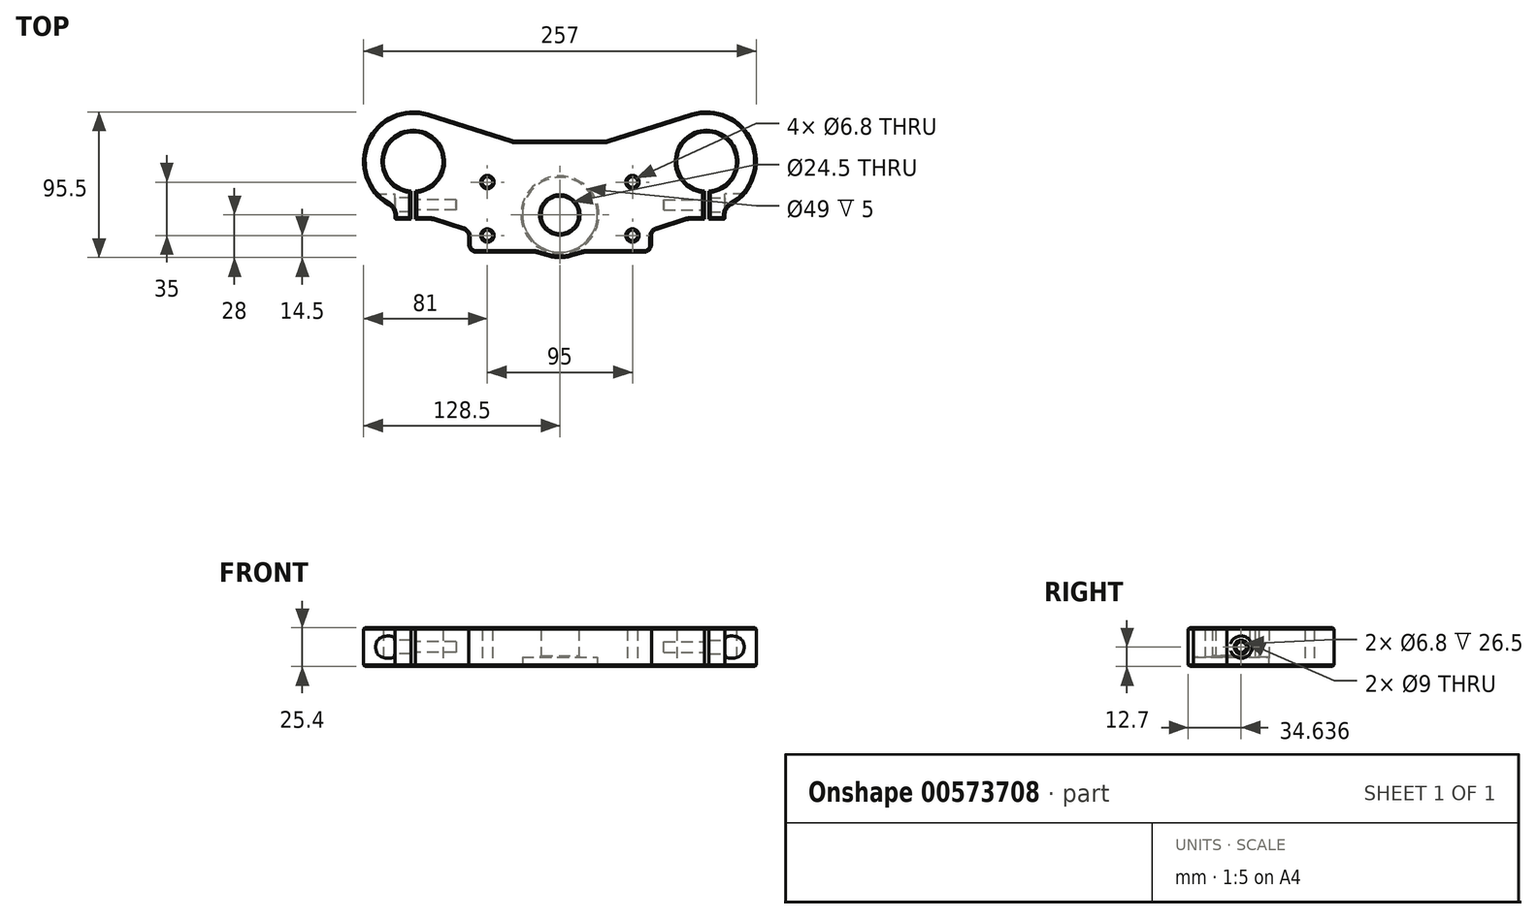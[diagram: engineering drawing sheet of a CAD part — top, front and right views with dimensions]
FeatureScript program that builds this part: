
annotation { "Feature Type Name" : "Feature", "Feature Type Description" : "" }
export const myFeature = defineFeature(function(context is Context, id is Id, definition is map)
    precondition{}
    {
        {
            var Q0;
            Q0=qCreatedBy(makeId("Top.planeOp"),FACE);
            var sketch = newSketch(context, id + "F0", { "sketchPlane" : qUnion([Q0])});
            skArc(sketch, "E0", {"start": v(-115.44, 16) * mm, "mid": v(-109.79, 3.71) * mm, "end": v(-97.5, -1.94) * mm});
            skArc(sketch, "E1", {"start": v(115.44, 19) * mm, "mid": v(82.21, 31.29) * mm, "end": v(94.5, -1.94) * mm});
            skCircle(sketch, "E2", {"center": v(0, -17.5) * mm, "radius": 12.25 * mm});
            skArc(sketch, "E3", {"start": v(108, -12.7) * mm, "mid": v(118.98, -5.48) * mm, "end": v(126.2, 5.5) * mm});
            skArc(sketch, "E4", {"start": v(-8.42, -44.2) * mm, "mid": v(0, -45.5) * mm, "end": v(8.42, -44.2) * mm});
            skLineSegment(sketch, "E5", {"start": v(-84, -20.36) * mm, "end": v(-59.7, -28.03) * mm});
            skLineSegment(sketch, "E6", {"start": v(84, -20.36) * mm, "end": v(59.9, -27.96) * mm});
            skLineSegment(sketch, "E7", {"start": v(-96, 17.5) * mm, "end": v(-150.04, 17.5) * mm, "construction": true});
            skLineSegment(sketch, "E8", {"start": v(-86.22, 48.5) * mm, "end": v(-29.97, 30.75) * mm});
            skLineSegment(sketch, "E9", {"start": v(86.22, 48.5) * mm, "end": v(29.97, 30.75) * mm});
            skLineSegment(sketch, "E10", {"start": v(-29.97, 30.75) * mm, "end": v(29.97, 30.75) * mm});
            skCircle(sketch, "E11", {"center": v(-47.5, 4) * mm, "radius": 3.4 * mm});
            skCircle(sketch, "E12", {"center": v(47.5, 4) * mm, "radius": 3.4 * mm});
            skCircle(sketch, "E13", {"center": v(-47.5, -31) * mm, "radius": 3.4 * mm});
            skCircle(sketch, "E14", {"center": v(47.5, -31) * mm, "radius": 3.4 * mm});
            skPoint(sketch, "E15.orphan", {"position": v(-108.6, 29.5) * mm});
            skPoint(sketch, "E16.orphan", {"position": v(-108.6, 5.5) * mm});
            skArc(sketch, "E17.trimOffspring", {"start": v(-86.22, 48.5) * mm, "mid": v(-109.95, 46.86) * mm, "end": v(-126.2, 29.5) * mm});
            skPoint(sketch, "E18.orphan", {"position": v(-148.56, 0) * mm});
            skPoint(sketch, "E19.MirrorCS.end.orphan", {"position": v(108.6, 5.5) * mm});
            skPoint(sketch, "E19.MirrorCS.start.orphan", {"position": v(108.6, 29.5) * mm});
            skArc(sketch, "E20.trimOffspring", {"start": v(-126.2, 5.5) * mm, "mid": v(-118.98, -5.48) * mm, "end": v(-108, -12.7) * mm});
            skArc(sketch, "E21.trimOffspring", {"start": v(126.2, 29.5) * mm, "mid": v(109.95, 46.86) * mm, "end": v(86.22, 48.5) * mm});
            skLineSegment(sketch, "E22", {"start": v(-47.5, 4) * mm, "end": v(-47.5, -31.88) * mm, "construction": true});
            skLineSegment(sketch, "E23", {"start": v(-47.5, -31.88) * mm, "end": v(95.24, -31.88) * mm, "construction": true});
            skLineSegment(sketch, "E24", {"start": v(-47.5, 4) * mm, "end": v(-47.5, 60.65) * mm, "construction": true});
            skLineSegment(sketch, "E25", {"start": v(47.5, -31) * mm, "end": v(47.5, 56.36) * mm, "construction": true});
            skLineSegment(sketch, "E26", {"start": v(-47.5, 36.28) * mm, "end": v(47.5, 36.28) * mm, "construction": true});
            skPoint(sketch, "E26.startSnap0", {"position": v(-47.5, 32.32) * mm});
            skLineSegment(sketch, "E27", {"start": v(-57.1, -42) * mm, "end": v(-15.4, -42) * mm});
            skLineSegment(sketch, "E28.trimOffspring", {"start": v(15.4, -42) * mm, "end": v(57.1, -42) * mm});
            skLineSegment(sketch, "E29.trimOffspring", {"start": v(-15.4, -42) * mm, "end": v(-8.42, -44.2) * mm});
            skLineSegment(sketch, "E30.trimOffspring", {"start": v(-47.5, -34.4) * mm, "end": v(-47.5, -34.52) * mm, "construction": true});
            skLineSegment(sketch, "E31.trimOffspring", {"start": v(15.4, -42) * mm, "end": v(8.42, -44.2) * mm});
            skArc(sketch, "E32", {"start": v(-126.2, 29.5) * mm, "mid": v(-128.5, 17.5) * mm, "end": v(-126.2, 5.5) * mm});
            skPoint(sketch, "E33.left.start.orphan", {"position": v(-134.5, 29.5) * mm});
            skPoint(sketch, "E33.top.start.orphan", {"position": v(-134.5, 5.5) * mm});
            skArc(sketch, "E34", {"start": v(-115.44, 19) * mm, "mid": v(-115.5, 17.5) * mm, "end": v(-115.44, 16) * mm});
            skArc(sketch, "E35", {"start": v(115.44, 19) * mm, "mid": v(115.49, 18.25) * mm, "end": v(115.5, 17.5) * mm});
            skArc(sketch, "E36", {"start": v(126.2, 29.5) * mm, "mid": v(128.5, 17.5) * mm, "end": v(126.2, 5.5) * mm});
            skArc(sketch, "E37", {"start": v(115.44, 16) * mm, "mid": v(115.49, 16.75) * mm, "end": v(115.5, 17.5) * mm});
            skLineSegment(sketch, "E38", {"start": v(-96, 17.5) * mm, "end": v(-96, -58.97) * mm, "construction": true});
            skLineSegment(sketch, "E39.top", {"start": v(-108, -20.36) * mm, "end": v(-97.5, -20.36) * mm});
            skLineSegment(sketch, "E39.left", {"start": v(-108, -12.7) * mm, "end": v(-108, -20.36) * mm});
            skLineSegment(sketch, "E40.MirrorCS", {"start": v(108, -20.36) * mm, "end": v(97.5, -20.36) * mm});
            skLineSegment(sketch, "E41.MirrorCS", {"start": v(108, -12.7) * mm, "end": v(108, -20.36) * mm});
            skPoint(sketch, "E42.orphan", {"position": v(105.78, -13.5) * mm});
            skLineSegment(sketch, "E43.left", {"start": v(-97.5, -1.94) * mm, "end": v(-97.5, -20.36) * mm});
            skLineSegment(sketch, "E43.right", {"start": v(-94.5, -1.94) * mm, "end": v(-94.5, -20.36) * mm});
            skLineSegment(sketch, "E44.left", {"start": v(94.5, -1.94) * mm, "end": v(94.5, -20.36) * mm});
            skLineSegment(sketch, "E44.right", {"start": v(97.5, -1.94) * mm, "end": v(97.5, -20.36) * mm});
            skLineSegment(sketch, "E45", {"start": v(96, 17.5) * mm, "end": v(96, -38.63) * mm, "construction": true});
            skPoint(sketch, "E45.endSnap0", {"position": v(96, -20.36) * mm});
            skArc(sketch, "E46.trimOffspring", {"start": v(-94.5, -1.94) * mm, "mid": v(-82.21, 31.29) * mm, "end": v(-115.44, 19) * mm});
            skLineSegment(sketch, "E47.trimOffspring", {"start": v(-94.5, -20.36) * mm, "end": v(-84, -20.36) * mm});
            skLineSegment(sketch, "E48.trimOffspring", {"start": v(94.5, -20.36) * mm, "end": v(84, -20.36) * mm});
            skArc(sketch, "E49.trimOffspring", {"start": v(97.5, -1.94) * mm, "mid": v(109.79, 3.71) * mm, "end": v(115.44, 16) * mm});
            skLineSegment(sketch, "E50", {"start": v(-57.1, -42) * mm, "end": v(-59.7, -42) * mm});
            skLineSegment(sketch, "E51", {"start": v(-59.7, -42) * mm, "end": v(-59.7, -28.03) * mm});
            skLineSegment(sketch, "E52", {"start": v(57.1, -42) * mm, "end": v(59.9, -42) * mm});
            skLineSegment(sketch, "E53", {"start": v(59.9, -42) * mm, "end": v(59.9, -27.96) * mm});
            skPoint(sketch, "E54.orphan", {"position": v(57.1, -28.85) * mm});
            skSolve(sketch);
        }
        {
            var Q0;
            Q0 = qSketchRegion(id + "F0", true);
            extrude(context, id + "F1", {"entities" : qUnion([Q0]), "depth" : 25.4 * mm, "offsetDistance" : 25 * mm});
        }
        {
            var Q0;
            Q0=makeQuery(id+"F1.opExtrude","CAP_FACE",FACE,{"disambiguationData":[OSD([sQuery(id+"F0.wireOp",EDGE,"E0"),sQuery(id+"F0.wireOp",EDGE,"E1"),sQuery(id+"F0.wireOp",EDGE,"E2"),sQuery(id+"F0.wireOp",EDGE,"E3"),sQuery(id+"F0.wireOp",EDGE,"E4"),sQuery(id+"F0.wireOp",EDGE,"E5"),sQuery(id+"F0.wireOp",EDGE,"E6"),sQuery(id+"F0.wireOp",EDGE,"E33.bottom"),sQuery(id+"F0.wireOp",EDGE,"E33.top"),sQuery(id+"F0.wireOp",EDGE,"E33.left"),sQuery(id+"F0.wireOp",EDGE,"f1757bc2-bd20-4476-96d3-2265b81b4f2b0.MirrorCS"),sQuery(id+"F0.wireOp",EDGE,"775a69b1-2f4f-49db-8b7b-db785da90cee0.MirrorCS"),sQuery(id+"F0.wireOp",EDGE,"3ec31bf6-936d-4883-9dcf-82827e0fa2ad0.MirrorCS"),sQuery(id+"F0.wireOp",EDGE,"E8"),sQuery(id+"F0.wireOp",EDGE,"E9"),sQuery(id+"F0.wireOp",EDGE,"E10"),sQuery(id+"F0.wireOp",EDGE,"E11"),sQuery(id+"F0.wireOp",EDGE,"E12"),sQuery(id+"F0.wireOp",EDGE,"E13"),sQuery(id+"F0.wireOp",EDGE,"E14"),sQuery(id+"F0.wireOp",EDGE,"E17.trimOffspring"),sQuery(id+"F0.wireOp",EDGE,"dbH54HY8-ATN7-0WNP-fYwK-wR0IxBY40SBz.bottom"),sQuery(id+"F0.wireOp",EDGE,"dbH54HY8-ATN7-0WNP-fYwK-wR0IxBY40SBz.top"),sQuery(id+"F0.wireOp",EDGE,"3AyZsfYV-9XAQ-6Yzz-t8sR-OLsTKYj4z3ro.bottom"),sQuery(id+"F0.wireOp",EDGE,"3AyZsfYV-9XAQ-6Yzz-t8sR-OLsTKYj4z3ro.top"),sQuery(id+"F0.wireOp",EDGE,"b436fade-894c-4302-851f-ed3abdfff13f.trimOffspring"),sQuery(id+"F0.wireOp",EDGE,"E20.trimOffspring"),sQuery(id+"F0.wireOp",EDGE,"c79fd97f-b23e-4375-80a9-bfeef2d48203.trimOffspring"),sQuery(id+"F0.wireOp",EDGE,"E21.trimOffspring")])],"isStart":true});
            var sketch = newSketch(context, id + "F2", { "sketchPlane" : qUnion([Q0])});
            skCircle(sketch, "E55", {"center": v(0, 17.5) * mm, "radius": 24.5 * mm});
            skSolve(sketch);
        }
        {
            var Q0;
            Q0 = qSketchRegion(id + "F2", true);
            extrude(context, id + "F3", {"entities" : qUnion([Q0]), "operationType" : NewBodyOperationType.REMOVE, "oppositeDirection" : true, "depth" : 6 * mm, "offsetDistance" : 25 * mm});
        }
        {
            var Q0;
            Q0=makeQuery(id+"F1.opExtrude","SWEPT_FACE",FACE,{"disambiguationData":[OSD([sQuery(id+"F0.wireOp",EDGE,"E39.left")])]});
            var sketch = newSketch(context, id + "F4", { "sketchPlane" : qUnion([Q0])});
            skCircle(sketch, "E56", {"center": v(10.86, 12.7) * mm, "radius": 3.4 * mm});
            skSolve(sketch);
        }
        {
            var Q0;
            Q0 = qSketchRegion(id + "F4", true);
            extrude(context, id + "F5", {"entities" : qUnion([Q0]), "operationType" : NewBodyOperationType.REMOVE, "oppositeDirection" : true, "depth" : 40 * mm, "offsetDistance" : 25 * mm, "hasSecondDirection" : true, "secondDirectionOppositeDirection" : false, "secondDirectionDepth" : 8 * mm});
        }
        {
            var Q0;
            Q0=makeQuery(id+"F1.opExtrude","SWEPT_FACE",FACE,{"disambiguationData":[OSD([sQuery(id+"F0.wireOp",EDGE,"E39.left")])]});
            var sketch = newSketch(context, id + "F6", { "sketchPlane" : qUnion([Q0])});
            skCircle(sketch, "E57", {"center": v(10.86, 12.7) * mm, "radius": 7.25 * mm});
            skSolve(sketch);
        }
        {
            var Q0;
            Q0 = qSketchRegion(id + "F6", true);
            extrude(context, id + "F7", {"entities" : qUnion([Q0]), "operationType" : NewBodyOperationType.REMOVE, "oppositeDirection" : true, "depth" : 0 * mm, "offsetDistance" : 25 * mm, "hasSecondDirection" : true, "secondDirectionOppositeDirection" : false, "secondDirectionDepth" : 25 * mm});
        }
        {
            var Q0;
            Q0=makeQuery(id+"F1.opExtrude","SWEPT_FACE",FACE,{"disambiguationData":[OSD([sQuery(id+"F0.wireOp",EDGE,"E41.MirrorCS")])]});
            var sketch = newSketch(context, id + "F8", { "sketchPlane" : qUnion([Q0])});
            skCircle(sketch, "E58", {"center": v(-10.86, 12.7) * mm, "radius": 3.4 * mm});
            skSolve(sketch);
        }
        {
            var Q0;
            Q0 = qSketchRegion(id + "F8", true);
            extrude(context, id + "F9", {"entities" : qUnion([Q0]), "operationType" : NewBodyOperationType.REMOVE, "oppositeDirection" : true, "depth" : 40 * mm, "offsetDistance" : 25 * mm, "hasSecondDirection" : true, "secondDirectionOppositeDirection" : false, "secondDirectionDepth" : 25 * mm});
        }
        {
            var Q0;
            Q0=makeQuery(id+"F1.opExtrude","SWEPT_FACE",FACE,{"disambiguationData":[OSD([sQuery(id+"F0.wireOp",EDGE,"E41.MirrorCS")])]});
            var sketch = newSketch(context, id + "F10", { "sketchPlane" : qUnion([Q0])});
            skCircle(sketch, "E59", {"center": v(-10.86, 12.7) * mm, "radius": 7.25 * mm});
            skSolve(sketch);
        }
        {
            var Q0;
            Q0 = qSketchRegion(id + "F10", true);
            extrude(context, id + "F11", {"entities" : qUnion([Q0]), "operationType" : NewBodyOperationType.REMOVE, "depth" : 25 * mm, "offsetDistance" : 25 * mm});
        }
        {
            var Q0;
            Q0=makeQuery(id+"F1.opExtrude","SWEPT_EDGE",EDGE,{"disambiguationData":[OSD([sQuery(id+"F0.wireOp",EDGE,"E33.bottom"),sQuery(id+"F0.wireOp",EDGE,"E17.trimOffspring")])]});
            var Q1;
            Q1=makeQuery(id+"F1.opExtrude","SWEPT_EDGE",EDGE,{"disambiguationData":[OSD([sQuery(id+"F0.wireOp",EDGE,"E8"),sQuery(id+"F0.wireOp",EDGE,"E10")])]});
            var Q2;
            Q2=makeQuery(id+"F1.opExtrude","SWEPT_EDGE",EDGE,{"disambiguationData":[OSD([sQuery(id+"F0.wireOp",EDGE,"E9"),sQuery(id+"F0.wireOp",EDGE,"E10")])]});
            var Q3;
            Q3=makeQuery(id+"F1.opExtrude","SWEPT_EDGE",EDGE,{"disambiguationData":[OSD([sQuery(id+"F0.wireOp",EDGE,"f1757bc2-bd20-4476-96d3-2265b81b4f2b0.MirrorCS"),sQuery(id+"F0.wireOp",EDGE,"E21.trimOffspring")])]});
            var Q4;
            Q4=makeQuery(id+"F1.opExtrude","SWEPT_EDGE",EDGE,{"disambiguationData":[OSD([sQuery(id+"F0.wireOp",EDGE,"E3"),sQuery(id+"F0.wireOp",EDGE,"775a69b1-2f4f-49db-8b7b-db785da90cee0.MirrorCS")])]});
            var Q5;
            Q5=makeQuery(id+"F1.opExtrude","SWEPT_EDGE",EDGE,{"disambiguationData":[OSD([sQuery(id+"F0.wireOp",EDGE,"E33.top"),sQuery(id+"F0.wireOp",EDGE,"E20.trimOffspring")])]});
            var Q6;
            Q6=makeQuery(id+"F1.opExtrude","SWEPT_EDGE",EDGE,{"disambiguationData":[OSD([sQuery(id+"F0.wireOp",EDGE,"E5"),sQuery(id+"F0.wireOp",EDGE,"E47.trimOffspring")])]});
            var Q7;
            Q7=makeQuery(id+"F1.opExtrude","SWEPT_EDGE",EDGE,{"disambiguationData":[OSD([sQuery(id+"F0.wireOp",EDGE,"E27"),sQuery(id+"F0.wireOp",EDGE,"z9qm4a1j-licB-j2B5-KDq9-BdoUQCzciK1D")])]});
            var Q8;
            Q8=makeQuery(id+"F1.opExtrude","SWEPT_EDGE",EDGE,{"disambiguationData":[OSD([sQuery(id+"F0.wireOp",EDGE,"E27"),sQuery(id+"F0.wireOp",EDGE,"E29.trimOffspring")])]});
            var Q9;
            Q9=makeQuery(id+"F1.opExtrude","SWEPT_EDGE",EDGE,{"disambiguationData":[OSD([sQuery(id+"F0.wireOp",EDGE,"E28.trimOffspring"),sQuery(id+"F0.wireOp",EDGE,"E31.trimOffspring")])]});
            var Q10;
            Q10=makeQuery(id+"F1.opExtrude","SWEPT_EDGE",EDGE,{"disambiguationData":[OSD([sQuery(id+"F0.wireOp",EDGE,"RDK05WNW-WhtB-5xZk-FXdk-pwDi68KHupZF"),sQuery(id+"F0.wireOp",EDGE,"E28.trimOffspring")])]});
            var Q11;
            Q11=makeQuery(id+"F1.opExtrude","SWEPT_EDGE",EDGE,{"disambiguationData":[OSD([sQuery(id+"F0.wireOp",EDGE,"E6"),sQuery(id+"F0.wireOp",EDGE,"E48.trimOffspring")])]});
            fillet(context, id + "F12", {"entities" : qUnion([Q0, Q1, Q2, Q3, Q4, Q5, Q6, Q7, Q8, Q9, Q10, Q11]), "radius" : 8 * mm, "tangentPropagation" : true, "allowEdgeOverflow" : false});
        }
        {
            var Q0;
            Q0=makeQuery(id+"F1.opExtrude","SWEPT_EDGE",EDGE,{"disambiguationData":[OSD([sQuery(id+"F0.wireOp",EDGE,"E5"),sQuery(id+"F0.wireOp",EDGE,"z9qm4a1j-licB-j2B5-KDq9-BdoUQCzciK1D")])]});
            var Q1;
            Q1=makeQuery(id+"F1.opExtrude","SWEPT_EDGE",EDGE,{"disambiguationData":[OSD([sQuery(id+"F0.wireOp",EDGE,"E6"),sQuery(id+"F0.wireOp",EDGE,"RDK05WNW-WhtB-5xZk-FXdk-pwDi68KHupZF")])]});
            var Q2;
            Q2=makeQuery(id+"F1.opExtrude","SWEPT_EDGE",EDGE,{"disambiguationData":[OSD([sQuery(id+"F0.wireOp",EDGE,"E50"),sQuery(id+"F0.wireOp",EDGE,"E51")])]});
            var Q3;
            Q3=makeQuery(id+"F1.opExtrude","SWEPT_EDGE",EDGE,{"disambiguationData":[OSD([sQuery(id+"F0.wireOp",EDGE,"E52"),sQuery(id+"F0.wireOp",EDGE,"E53")])]});
            fillet(context, id + "F13", {"entities" : qUnion([Q0, Q1, Q2, Q3]), "radius" : 5 * mm, "tangentPropagation" : true, "allowEdgeOverflow" : false});
        }
        {
            var Q0;
            Q0=makeQuery(id+"F1.opExtrude","SWEPT_EDGE",EDGE,{"disambiguationData":[OSD([sQuery(id+"F0.wireOp",EDGE,"E40.MirrorCS"),sQuery(id+"F0.wireOp",EDGE,"E41.MirrorCS")])]});
            var Q1;
            Q1=makeQuery(id+"F1.opExtrude","SWEPT_EDGE",EDGE,{"disambiguationData":[OSD([sQuery(id+"F0.wireOp",EDGE,"E39.top"),sQuery(id+"F0.wireOp",EDGE,"E39.left")])]});
            fillet(context, id + "F14", {"entities" : qUnion([Q0, Q1]), "radius" : 1 * mm, "tangentPropagation" : true, "allowEdgeOverflow" : false});
        }
        {
            var Q0;
            Q0=makeQuery(id+"F1.opExtrude","CAP_FACE",FACE,{"disambiguationData":[OSD([sQuery(id+"F0.wireOp",EDGE,"E0"),sQuery(id+"F0.wireOp",EDGE,"E1"),sQuery(id+"F0.wireOp",EDGE,"E2"),sQuery(id+"F0.wireOp",EDGE,"E3"),sQuery(id+"F0.wireOp",EDGE,"E4"),sQuery(id+"F0.wireOp",EDGE,"E5"),sQuery(id+"F0.wireOp",EDGE,"E6"),sQuery(id+"F0.wireOp",EDGE,"E8"),sQuery(id+"F0.wireOp",EDGE,"E9"),sQuery(id+"F0.wireOp",EDGE,"E10"),sQuery(id+"F0.wireOp",EDGE,"E11"),sQuery(id+"F0.wireOp",EDGE,"E12"),sQuery(id+"F0.wireOp",EDGE,"E13"),sQuery(id+"F0.wireOp",EDGE,"E14"),sQuery(id+"F0.wireOp",EDGE,"E17.trimOffspring"),sQuery(id+"F0.wireOp",EDGE,"E20.trimOffspring"),sQuery(id+"F0.wireOp",EDGE,"E21.trimOffspring"),sQuery(id+"F0.wireOp",EDGE,"E27"),sQuery(id+"F0.wireOp",EDGE,"z9qm4a1j-licB-j2B5-KDq9-BdoUQCzciK1D"),sQuery(id+"F0.wireOp",EDGE,"RDK05WNW-WhtB-5xZk-FXdk-pwDi68KHupZF"),sQuery(id+"F0.wireOp",EDGE,"E28.trimOffspring"),sQuery(id+"F0.wireOp",EDGE,"E29.trimOffspring"),sQuery(id+"F0.wireOp",EDGE,"E31.trimOffspring"),sQuery(id+"F0.wireOp",EDGE,"E32"),sQuery(id+"F0.wireOp",EDGE,"E34"),sQuery(id+"F0.wireOp",EDGE,"E35"),sQuery(id+"F0.wireOp",EDGE,"E36"),sQuery(id+"F0.wireOp",EDGE,"E37"),sQuery(id+"F0.wireOp",EDGE,"E39.top"),sQuery(id+"F0.wireOp",EDGE,"E39.left"),sQuery(id+"F0.wireOp",EDGE,"E40.MirrorCS"),sQuery(id+"F0.wireOp",EDGE,"E41.MirrorCS"),sQuery(id+"F0.wireOp",EDGE,"E43.left"),sQuery(id+"F0.wireOp",EDGE,"E43.right"),sQuery(id+"F0.wireOp",EDGE,"E44.left"),sQuery(id+"F0.wireOp",EDGE,"E44.right"),sQuery(id+"F0.wireOp",EDGE,"E46.trimOffspring"),sQuery(id+"F0.wireOp",EDGE,"E47.trimOffspring"),sQuery(id+"F0.wireOp",EDGE,"E48.trimOffspring"),sQuery(id+"F0.wireOp",EDGE,"E49.trimOffspring")])],"isStart":false});
            var Q1;
            Q1=makeQuery(id+"F1.opExtrude","CAP_FACE",FACE,{"disambiguationData":[OSD([sQuery(id+"F0.wireOp",EDGE,"E0"),sQuery(id+"F0.wireOp",EDGE,"E1"),sQuery(id+"F0.wireOp",EDGE,"E2"),sQuery(id+"F0.wireOp",EDGE,"E3"),sQuery(id+"F0.wireOp",EDGE,"E4"),sQuery(id+"F0.wireOp",EDGE,"E5"),sQuery(id+"F0.wireOp",EDGE,"E6"),sQuery(id+"F0.wireOp",EDGE,"E8"),sQuery(id+"F0.wireOp",EDGE,"E9"),sQuery(id+"F0.wireOp",EDGE,"E10"),sQuery(id+"F0.wireOp",EDGE,"E11"),sQuery(id+"F0.wireOp",EDGE,"E12"),sQuery(id+"F0.wireOp",EDGE,"E13"),sQuery(id+"F0.wireOp",EDGE,"E14"),sQuery(id+"F0.wireOp",EDGE,"E17.trimOffspring"),sQuery(id+"F0.wireOp",EDGE,"E20.trimOffspring"),sQuery(id+"F0.wireOp",EDGE,"E21.trimOffspring"),sQuery(id+"F0.wireOp",EDGE,"E27"),sQuery(id+"F0.wireOp",EDGE,"z9qm4a1j-licB-j2B5-KDq9-BdoUQCzciK1D"),sQuery(id+"F0.wireOp",EDGE,"RDK05WNW-WhtB-5xZk-FXdk-pwDi68KHupZF"),sQuery(id+"F0.wireOp",EDGE,"E28.trimOffspring"),sQuery(id+"F0.wireOp",EDGE,"E29.trimOffspring"),sQuery(id+"F0.wireOp",EDGE,"E31.trimOffspring"),sQuery(id+"F0.wireOp",EDGE,"E32"),sQuery(id+"F0.wireOp",EDGE,"E34"),sQuery(id+"F0.wireOp",EDGE,"E35"),sQuery(id+"F0.wireOp",EDGE,"E36"),sQuery(id+"F0.wireOp",EDGE,"E37"),sQuery(id+"F0.wireOp",EDGE,"E39.top"),sQuery(id+"F0.wireOp",EDGE,"E39.left"),sQuery(id+"F0.wireOp",EDGE,"E40.MirrorCS"),sQuery(id+"F0.wireOp",EDGE,"E41.MirrorCS"),sQuery(id+"F0.wireOp",EDGE,"E43.left"),sQuery(id+"F0.wireOp",EDGE,"E43.right"),sQuery(id+"F0.wireOp",EDGE,"E44.left"),sQuery(id+"F0.wireOp",EDGE,"E44.right"),sQuery(id+"F0.wireOp",EDGE,"E46.trimOffspring"),sQuery(id+"F0.wireOp",EDGE,"E47.trimOffspring"),sQuery(id+"F0.wireOp",EDGE,"E48.trimOffspring"),sQuery(id+"F0.wireOp",EDGE,"E49.trimOffspring")])],"isStart":true});
            chamfer(context, id + "F15", {"entities" : qUnion([Q0, Q1]), "width" : 1 * mm, "tangentPropagation" : true});
        }
        {
            var Q0;
            Q0=makeQuery(id+"F3.boolean.opBoolean","INTERSECT",EDGE,{"derivedFrom":[makeQuery(id+"F1.opExtrude","SWEPT_FACE",FACE,{"disambiguationData":[OSD([sQuery(id+"F0.wireOp",EDGE,"E2")])]}),makeQuery(id+"F3.opExtrude","CAP_FACE",FACE,{"disambiguationData":[OSD([sQuery(id+"F2.wireOp",EDGE,"E55")])],"isStart":false})]});
            chamfer(context, id + "F16", {"entities" : qUnion([Q0]), "width" : 1 * mm, "tangentPropagation" : true});
        }
        {
            var Q0;
            Q0=makeQuery(id+"F11.boolean.opBoolean","MERGE",FACE,{"derivedFrom":[makeQuery(id+"F1.opExtrude","SWEPT_FACE",FACE,{"disambiguationData":[OSD([sQuery(id+"F0.wireOp",EDGE,"E41.MirrorCS")])]}),makeQuery(id+"F11.opExtrude","CAP_FACE",FACE,{"disambiguationData":[OSD([sQuery(id+"F10.wireOp",EDGE,"E59")])],"isStart":true})]});
            var sketch = newSketch(context, id + "F17", { "sketchPlane" : qUnion([Q0])});
            skCircle(sketch, "E60", {"center": v(-10.86, 12.7) * mm, "radius": 4.5 * mm});
            skSolve(sketch);
        }
        {
            var Q0;
            Q0 = qSketchRegion(id + "F17", true);
            var Q1;
            Q1=makeQuery(id+"F1.opExtrude","SWEPT_FACE",FACE,{"disambiguationData":[OSD([sQuery(id+"F0.wireOp",EDGE,"E44.right")])]});
            extrude(context, id + "F18", {"entities" : qUnion([Q0]), "operationType" : NewBodyOperationType.REMOVE, "endBound" : BoundingType.UP_TO_SURFACE, "oppositeDirection" : true, "depth" : 25 * mm, "endBoundEntityFace" : qUnion([Q1]), "offsetDistance" : 25 * mm});
        }
        {
            var Q0;
            Q0=makeQuery(id+"F7.boolean.opBoolean","MERGE",FACE,{"derivedFrom":[makeQuery(id+"F1.opExtrude","SWEPT_FACE",FACE,{"disambiguationData":[OSD([sQuery(id+"F0.wireOp",EDGE,"E39.left")])]}),makeQuery(id+"F7.opExtrude","CAP_FACE",FACE,{"disambiguationData":[OSD([sQuery(id+"F6.wireOp",EDGE,"E57")])],"isStart":false})]});
            var sketch = newSketch(context, id + "F19", { "sketchPlane" : qUnion([Q0])});
            skCircle(sketch, "E61", {"center": v(10.86, 12.7) * mm, "radius": 4.5 * mm});
            skSolve(sketch);
        }
        {
            var Q0;
            Q0 = qSketchRegion(id + "F19", true);
            var Q1;
            Q1=makeQuery(id+"F1.opExtrude","SWEPT_FACE",FACE,{"disambiguationData":[OSD([sQuery(id+"F0.wireOp",EDGE,"E43.left")])]});
            extrude(context, id + "F20", {"entities" : qUnion([Q0]), "operationType" : NewBodyOperationType.REMOVE, "endBound" : BoundingType.UP_TO_SURFACE, "oppositeDirection" : true, "depth" : 25 * mm, "endBoundEntityFace" : qUnion([Q1]), "offsetDistance" : 25 * mm});
        }
    });
